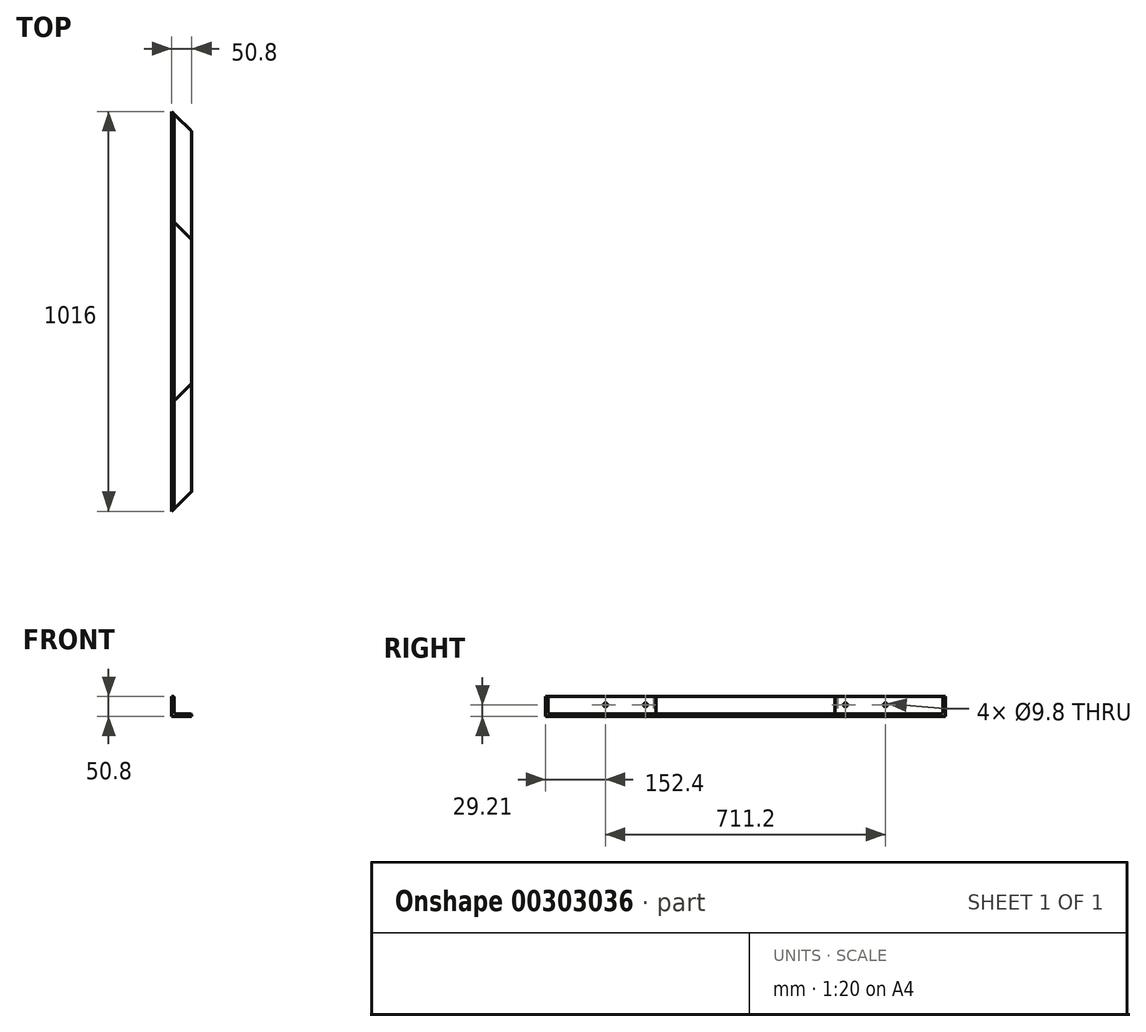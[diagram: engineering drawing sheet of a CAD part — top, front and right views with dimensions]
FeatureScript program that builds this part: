
annotation { "Feature Type Name" : "Feature", "Feature Type Description" : "" }
export const myFeature = defineFeature(function(context is Context, id is Id, definition is map)
    precondition{}
    {
        {
            var Q0;
            Q0=qCreatedBy(makeId("Front.planeOp"),FACE);
            var sketch = newSketch(context, id + "F0", { "sketchPlane" : qUnion([Q0])});
            skLineSegment(sketch, "E0", {"start": v(0, 0) * mm, "end": v(50.8, 0) * mm});
            skLineSegment(sketch, "E1", {"start": v(50.8, 0) * mm, "end": v(50.8, 3.17) * mm});
            skArc(sketch, "E2", {"start": v(50.8, 3.17) * mm, "mid": v(49.87, 5.42) * mm, "end": v(47.63, 6.35) * mm});
            skLineSegment(sketch, "E3", {"start": v(47.63, 6.35) * mm, "end": v(12.7, 6.35) * mm});
            skArc(sketch, "E4", {"start": v(12.7, 6.35) * mm, "mid": v(8.2, 8.2) * mm, "end": v(6.35, 12.7) * mm});
            skLineSegment(sketch, "E5", {"start": v(6.35, 12.7) * mm, "end": v(6.35, 47.63) * mm});
            skArc(sketch, "E6", {"start": v(6.35, 47.63) * mm, "mid": v(5.42, 49.87) * mm, "end": v(3.17, 50.8) * mm});
            skLineSegment(sketch, "E7", {"start": v(3.17, 50.8) * mm, "end": v(0, 50.8) * mm});
            skLineSegment(sketch, "E8", {"start": v(0, 50.8) * mm, "end": v(0, 0) * mm});
            skSolve(sketch);
        }
        {
            var Q0;
            Q0=makeQuery(id+"F0.imprint","IMPRINT",FACE,{"disambiguationData":[TD([[makeQuery(id+"F0.imprint","IMPRINT",EDGE,{"derivedFrom":sQuery(id+"F0.wireOp",EDGE,"E0")}),1.0]])]});
            extrude(context, id + "F1", {"entities" : qUnion([Q0]), "depth" : 466.72 * mm, "symmetric" : true});
        }
        {
            var Q0;
            Q0=makeQuery(id+"F1.opExtrude","SWEPT_FACE",FACE,{"disambiguationData":[OSD([sQuery(id+"F0.wireOp",EDGE,"E0")])]});
            var sketch = newSketch(context, id + "F2", { "sketchPlane" : qUnion([Q0])});
            skLineSegment(sketch, "E9.0.0", {"start": v(0, -233.36) * mm, "end": v(50.8, -233.36) * mm});
            skLineSegment(sketch, "E9.0.1", {"start": v(50.8, -233.36) * mm, "end": v(50.8, 233.36) * mm});
            skLineSegment(sketch, "E9.0.2", {"start": v(50.8, 233.36) * mm, "end": v(0, 233.36) * mm});
            skLineSegment(sketch, "E9.0.3", {"start": v(0, 233.36) * mm, "end": v(0, -233.36) * mm});
            skLineSegment(sketch, "E10", {"start": v(0, 233.36) * mm, "end": v(50.8, 182.56) * mm});
            skLineSegment(sketch, "E11.MirrorCS", {"start": v(0, -233.36) * mm, "end": v(50.8, -182.56) * mm});
            skSolve(sketch);
        }
        {
            var Q0;
            {var subQ0=sQuery(id+"F2.wireOp",EDGE,"E9.0.2");Q0=makeQuery(id+"F2.imprint","IMPRINT",FACE,{"disambiguationData":[TD([[makeQuery(id+"F2.imprint","IMPRINT",EDGE,{"derivedFrom":subQ0}),-1.0]])]});}
            var Q1;
            {var subQ0=sQuery(id+"F2.wireOp",EDGE,"E9.0.0");Q1=makeQuery(id+"F2.imprint","IMPRINT",FACE,{"disambiguationData":[TD([[makeQuery(id+"F2.imprint","IMPRINT",EDGE,{"derivedFrom":subQ0}),1.0]])]});}
            extrude(context, id + "F3", {"entities" : qUnion([Q0, Q1]), "operationType" : NewBodyOperationType.REMOVE, "endBound" : BoundingType.THROUGH_ALL, "oppositeDirection" : true, "depth" : 25.4 * mm});
        }
        {
            var Q0;
            Q0=qSketchRegion(id+"F0",true);
            extrude(context, id + "F4", {"entities" : qUnion([Q0]), "depth" : 1016 * mm, "symmetric" : true});
        }
        {
            var Q0;
            Q0=makeQuery(id+"F4.opExtrude","SWEPT_FACE",FACE,{"disambiguationData":[OSD([sQuery(id+"F0.wireOp",EDGE,"E0")])]});
            var sketch = newSketch(context, id + "F5", { "sketchPlane" : qUnion([Q0])});
            skLineSegment(sketch, "E12", {"start": v(0, 508) * mm, "end": v(50.8, 457.2) * mm});
            skLineSegment(sketch, "E13.MirrorCS", {"start": v(0, -508) * mm, "end": v(50.8, -457.2) * mm});
            skSolve(sketch);
        }
        {
            var Q0;
            {var subQ0=sQuery(id+"F5.wireOp",EDGE,"E12");Q0=makeQuery(id+"F5.imprint","IMPRINT",FACE,{"disambiguationData":[TD([[makeQuery(id+"F5.imprint","IMPRINT",EDGE,{"derivedFrom":subQ0}),1.0]])]});}
            var Q1;
            {var subQ0=sQuery(id+"F5.wireOp",EDGE,"E13.MirrorCS");Q1=makeQuery(id+"F5.imprint","IMPRINT",FACE,{"disambiguationData":[TD([[makeQuery(id+"F5.imprint","IMPRINT",EDGE,{"derivedFrom":subQ0}),-1.0]])]});}
            extrude(context, id + "F6", {"entities" : qUnion([Q0, Q1]), "operationType" : NewBodyOperationType.REMOVE, "endBound" : BoundingType.THROUGH_ALL, "oppositeDirection" : true, "depth" : 25.4 * mm});
        }
        {
            var Q0;
            Q0=makeQuery(id+"F4.opExtrude","SWEPT_FACE",FACE,{"disambiguationData":[OSD([sQuery(id+"F0.wireOp",EDGE,"E8")])]});
            var sketch = newSketch(context, id + "F7", { "sketchPlane" : qUnion([Q0])});
            skLineSegment(sketch, "E14", {"start": v(-565.42, 29.21) * mm, "end": v(571.71, 29.21) * mm, "construction": true});
            skPoint(sketch, "E15", {"position": v(-355.6, 29.21) * mm});
            skPoint(sketch, "E16", {"position": v(-254, 29.21) * mm});
            skPoint(sketch, "E17", {"position": v(254, 29.21) * mm});
            skPoint(sketch, "E18", {"position": v(355.6, 29.21) * mm});
            skSolve(sketch);
        }
        {
            var Q0;
            Q0=sQuery(id+"F7.wireOp",VERTEX,"E18");
            var Q1;
            Q1=sQuery(id+"F7.wireOp",VERTEX,"E17");
            var Q2;
            Q2=sQuery(id+"F7.wireOp",VERTEX,"E16");
            var Q3;
            Q3=sQuery(id+"F7.wireOp",VERTEX,"E15");
            var Q4;
            Q4=makeQuery(id+"F4.opExtrude","SWEPT_BODY",BODY,{"disambiguationData":[OSD([sQuery(id+"F0.wireOp",EDGE,"E0"),sQuery(id+"F0.wireOp",EDGE,"E1"),sQuery(id+"F0.wireOp",EDGE,"E2"),sQuery(id+"F0.wireOp",EDGE,"E3"),sQuery(id+"F0.wireOp",EDGE,"E4"),sQuery(id+"F0.wireOp",EDGE,"E5"),sQuery(id+"F0.wireOp",EDGE,"E6"),sQuery(id+"F0.wireOp",EDGE,"E7"),sQuery(id+"F0.wireOp",EDGE,"E8")])]});
            hole(context, id + "F8", {"style" : HoleStyle.SIMPLE, "endStyle" : HoleEndStyle.THROUGH, "standardTappedOrClearance" : lookupTablePath({ "standard" : "ANSI", "fit" : "Close", "size" : "3/8", "type" : "Clearance" }), "standardBlindInLast" : lookupTablePath({ "fit" : "Close", "standard" : "ANSI", "size" : "3/8", "type" : "Clearance" }), "holeDiameter" : 9.8 * mm, "tappedDepth" : 12.7 * mm, "tapClearance" : 3, "locations" : qUnion([Q0, Q1, Q2, Q3]), "scope" : qUnion([Q4])});
        }
    });
